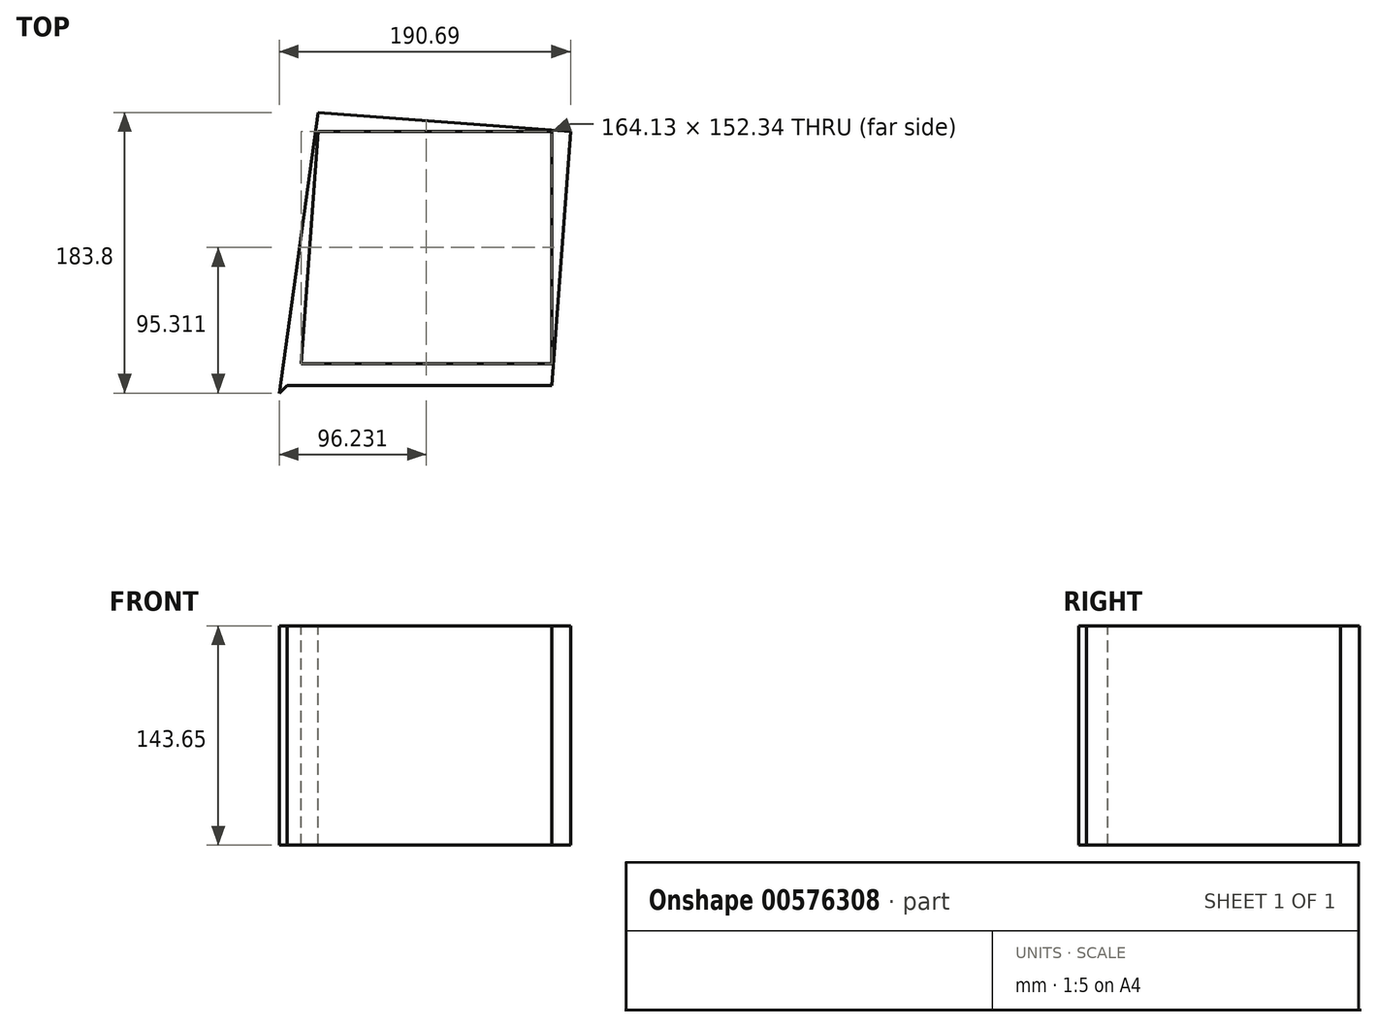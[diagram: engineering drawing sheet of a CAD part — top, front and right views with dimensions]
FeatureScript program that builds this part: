
annotation { "Feature Type Name" : "Feature", "Feature Type Description" : "" }
export const myFeature = defineFeature(function(context is Context, id is Id, definition is map)
    precondition{}
    {
        {
            var Q0;
            Q0=qCreatedBy(makeId("Top.planeOp"),FACE);
            var sketch = newSketch(context, id + "F0", { "sketchPlane" : qUnion([Q0])});
            skLineSegment(sketch, "E0", {"start": v(-80.97, -73.33) * mm, "end": v(83.15, -73.33) * mm});
            skLineSegment(sketch, "E1", {"start": v(83.15, -73.33) * mm, "end": v(83.15, 79) * mm});
            skLineSegment(sketch, "E2", {"start": v(83.15, 79) * mm, "end": v(-69.85, 79) * mm});
            skLineSegment(sketch, "E3", {"start": v(-69.85, 79) * mm, "end": v(-80.97, -73.33) * mm});
            skLineSegment(sketch, "E4", {"start": v(-94.58, -87.37) * mm, "end": v(83.15, -87.37) * mm});
            skLineSegment(sketch, "E5", {"start": v(83.15, -87.37) * mm, "end": v(95.55, 79) * mm});
            skLineSegment(sketch, "E6", {"start": v(95.55, 79) * mm, "end": v(-69.85, 91.33) * mm});
            skLineSegment(sketch, "E7", {"start": v(-69.85, 91.33) * mm, "end": v(-95.14, -92.47) * mm});
            skLineSegment(sketch, "E8", {"start": v(-95.14, -92.47) * mm, "end": v(-85.3, -82.73) * mm});
            skLineSegment(sketch, "E9", {"start": v(-85.3, -82.73) * mm, "end": v(-86.44, -78.08) * mm});
            skSolve(sketch);
        }
        {
            var Q0;
            Q0 = qSketchRegion(id + "F0", true);
            extrude(context, id + "F1", {"entities" : qUnion([Q0]), "oppositeDirection" : true, "depth" : 143.65 * mm, "offsetDistance" : 25.4 * mm});
        }
    });
